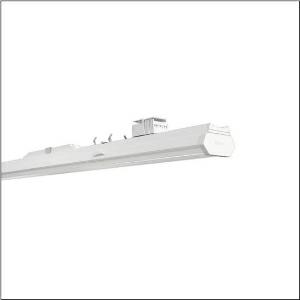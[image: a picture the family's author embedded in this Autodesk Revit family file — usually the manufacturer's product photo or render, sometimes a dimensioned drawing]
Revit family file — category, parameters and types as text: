
# Revit family: licross_r__11_protected_ho_51td11cn4exs_ee6c
name_source: partatom
category: Lighting Fixtures
units: mm (PartAtom-declared; Revit-internal decimal feet)

## family parameters
Cut with Voids When Loaded = No
Host = Face
Light Source = No
Part Type = Normal
Room Calculation Point = No
Round Connector Dimension = Use Diameter
Shared = No

## types (1)
- --- (1 x LED, 14460 lm, 77.6 W, 4000K)
    Apparent Load = 78 VA
    CIE Flux Codes = 84 94 98 99 100
    Color Rendering = 80
    Color Temperature = 4000K
    Default Elevation = 1800 mm
    Description = Licross® 11 Protected HO, luminaire insert, of sheet steel, galvanised, coil coated, white, length: 1.500mm, width: 90mm, height: 101mm, LED rated luminous flux: 14.460lm, light colour: 840, control gear: ON/OFF Multilumen, CLOi, with plug, 3-pole, with phase selection, mains connection: 220..240V, AC, 50/60Hz, halogen-free wiring, primary light control with lens, of plastic, primary optical cover: cover, of PMMA, light emission: direct with ceiling illumination distribution, primary light characteristic: symmetric, protection rating (complete): IP54, insulation class (complete): insulation class I (protective earthing), certification: CE, ENEC, VDE, UKCA, protection symbol: D if used in an environment with non-conductive dust loads with corresponding accessories, impact resistance: IK06, permissible ambient temperature for indoor applications: -35..+35°C, corresponds to IFS (International Featured Standards) requirements for safety and quality in the food industry, reducing of maximum allowable ambient temperature of 5°C with ceiling mounting, LABS conformity tested according to VDMA 24364:2018-05, packaging unit: 1 piece
    Height = 92 mm
    Lamp = 1 x LED
    Lamp Light Flux = 14460 lm
    Lamp Power = 77.6 W
    Lamp count = 1
    Length = 1500 mm
    Luminous efficacy = 186 lm/W
    Manufacturer = Siteco
    ModVariant = No
    Model = 51TD11CN4EXS
    Mounting Place = Ceiling
    Mounting Type = Pendant
    Number of Poles = 1
    OnlyDefault = Yes
    Power Factor = 1
    Product Name = Licross® 11 Protected HO
    Product group = luminaire insert
    ProductGroupID = 902
    Protection Class = Protection class I
    Protection Degree = IP 54
    RLX_Detail_Level = 1
    RlxData = <blob elided: 22057 chars, md5=2ad367e4>
    Socket = socket
    Standby Power = 0 W
    System Light Flux = 14460 lm
    System Power = 78 W
    Type Comments = factory setting: luminous flux: 100 % | (A | C | E) | 181 mA
    Type Image = l_1256145.jpg
    URL = http://relux.com
    VarID = @adj_003771
    Voltage = 0 V
    Weight = 0.00 kg
    Width = 88 mm

## geometry (parser evidence)
native form markers: Blend x4, Sweep x10
no freeform markers — native parametric forms only
